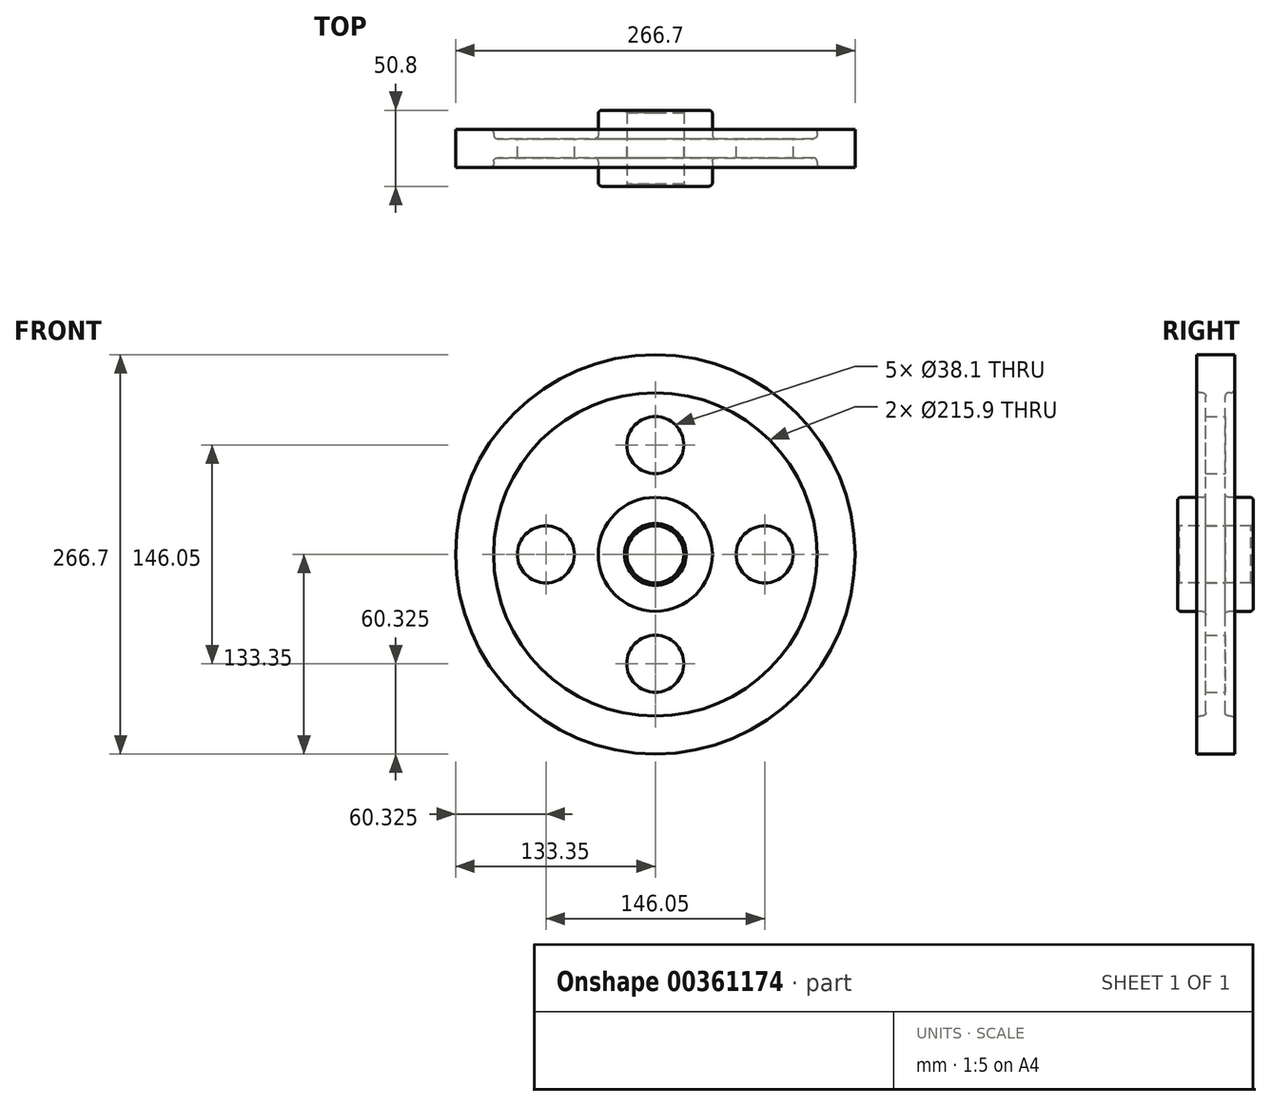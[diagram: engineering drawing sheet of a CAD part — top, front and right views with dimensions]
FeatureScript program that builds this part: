
annotation { "Feature Type Name" : "Feature", "Feature Type Description" : "" }
export const myFeature = defineFeature(function(context is Context, id is Id, definition is map)
    precondition{}
    {
        {
            var Q0;
            Q0=qCreatedBy(makeId("Right.planeOp"),FACE);
            var sketch = newSketch(context, id + "F0", { "sketchPlane" : qUnion([Q0])});
            skLineSegment(sketch, "E0", {"start": v(0, 0) * mm, "end": v(0, 28.58) * mm});
            skLineSegment(sketch, "E1", {"start": v(0, 28.58) * mm, "end": v(0, 73.03) * mm});
            skLineSegment(sketch, "E2", {"start": v(0, 73.03) * mm, "end": v(0, 120.65) * mm});
            skLineSegment(sketch, "E3", {"start": v(0, 0) * mm, "end": v(32.61, 0) * mm});
            skLineSegment(sketch, "E4.bottom", {"start": v(25.4, 19.05) * mm, "end": v(-25.4, 19.05) * mm});
            skLineSegment(sketch, "E4.top", {"start": v(25.4, 38.1) * mm, "end": v(6.35, 38.1) * mm});
            skLineSegment(sketch, "E4.left", {"start": v(25.4, 19.05) * mm, "end": v(25.4, 38.1) * mm});
            skLineSegment(sketch, "E4.right", {"start": v(-25.4, 19.05) * mm, "end": v(-25.4, 38.1) * mm});
            skPoint(sketch, "E4.middle", {"position": v(0, 28.58) * mm});
            skLineSegment(sketch, "E5.bottom", {"start": v(12.7, 107.95) * mm, "end": v(6.35, 107.95) * mm});
            skLineSegment(sketch, "E5.top", {"start": v(12.7, 133.35) * mm, "end": v(-12.7, 133.35) * mm});
            skLineSegment(sketch, "E5.left", {"start": v(12.7, 107.95) * mm, "end": v(12.7, 133.35) * mm});
            skLineSegment(sketch, "E5.right", {"start": v(-12.7, 107.95) * mm, "end": v(-12.7, 133.35) * mm});
            skPoint(sketch, "E5.middle", {"position": v(0, 120.65) * mm});
            skLineSegment(sketch, "E6.left", {"start": v(6.35, 35.07) * mm, "end": v(6.35, 110.98) * mm});
            skLineSegment(sketch, "E6.right", {"start": v(-6.35, 35.07) * mm, "end": v(-6.35, 110.98) * mm});
            skPoint(sketch, "E6.middle", {"position": v(0, 73.03) * mm});
            skLineSegment(sketch, "E7.trimOffspring", {"start": v(-6.35, 107.95) * mm, "end": v(-12.7, 107.95) * mm});
            skLineSegment(sketch, "E8.trimOffspring", {"start": v(-6.35, 38.1) * mm, "end": v(-25.4, 38.1) * mm});
            skSolve(sketch);
        }
        {
            var Q0;
            {var subQ4=sQuery(id+"F0.wireOp",EDGE,"E4.top");Q0=makeQuery(id+"F0.imprint","IMPRINT",FACE,{"disambiguationData":[TD([[makeQuery(id+"F0.imprint","IMPRINT",EDGE,{"derivedFrom":subQ4}),1.0]])]});}
            var Q1;
            Q1=sQuery(id+"F0.wireOp",EDGE,"E3");
            revolve(context, id + "F1", {"entities" : qUnion([Q0]), "axis" : qUnion([Q1]), "revolveType" : RevolveType.FULL});
        }
        {
            var Q0;
            Q0=makeQuery(id+"F1.opRevolve","SWEPT_FACE",FACE,{"disambiguationData":[OSD([sQuery(id+"F0.wireOp",EDGE,"E6.left")])]});
            var sketch = newSketch(context, id + "F2", { "sketchPlane" : qUnion([Q0])});
            skLineSegment(sketch, "E9", {"start": v(0, 0) * mm, "end": v(0, 73.03) * mm});
            skCircle(sketch, "E10", {"center": v(0, 73.03) * mm, "radius": 19.05 * mm});
            skCircle(sketch, "E11.1.0", {"center": v(-73.03, 0) * mm, "radius": 19.05 * mm});
            skCircle(sketch, "E11.2.0", {"center": v(0, -73.03) * mm, "radius": 19.05 * mm});
            skCircle(sketch, "E11.3.0", {"center": v(73.03, 0) * mm, "radius": 19.05 * mm});
            skPoint(sketch, "E11.center", {"position": v(0, 0) * mm});
            skSolve(sketch);
        }
        {
            var Q0;
            Q0=makeQuery(id+"F2.imprint","IMPRINT",FACE,{"disambiguationData":[TD([[makeQuery(id+"F2.imprint","IMPRINT",EDGE,{"derivedFrom":sQuery(id+"F2.wireOp",EDGE,"E10")}),1.0]])]});
            var Q1;
            Q1=makeQuery(id+"F2.imprint","IMPRINT",FACE,{"disambiguationData":[TD([[makeQuery(id+"F2.imprint","IMPRINT",EDGE,{"derivedFrom":sQuery(id+"F2.wireOp",EDGE,"E11.3.0")}),1.0]])]});
            var Q2;
            Q2=makeQuery(id+"F2.imprint","IMPRINT",FACE,{"disambiguationData":[TD([[makeQuery(id+"F2.imprint","IMPRINT",EDGE,{"derivedFrom":sQuery(id+"F2.wireOp",EDGE,"E11.2.0")}),1.0]])]});
            var Q3;
            Q3=makeQuery(id+"F2.imprint","IMPRINT",FACE,{"disambiguationData":[TD([[makeQuery(id+"F2.imprint","IMPRINT",EDGE,{"derivedFrom":sQuery(id+"F2.wireOp",EDGE,"E11.1.0")}),1.0]])]});
            extrude(context, id + "F3", {"entities" : qUnion([Q0, Q1, Q2, Q3]), "operationType" : NewBodyOperationType.REMOVE, "oppositeDirection" : true, "depth" : 25.4 * mm});
        }
        {
            var Q0;
            Q0=makeQuery(id+"F1.opRevolve","SWEPT_EDGE",EDGE,{"disambiguationData":[OSD([sQuery(id+"F0.wireOp",EDGE,"E6.right"),sQuery(id+"F0.wireOp",EDGE,"E7.trimOffspring")])]});
            var Q1;
            Q1=makeQuery(id+"F1.opRevolve","SWEPT_EDGE",EDGE,{"disambiguationData":[OSD([sQuery(id+"F0.wireOp",EDGE,"E5.right"),sQuery(id+"F0.wireOp",EDGE,"E7.trimOffspring")])]});
            var Q2;
            Q2=makeQuery(id+"F1.opRevolve","SWEPT_EDGE",EDGE,{"disambiguationData":[OSD([sQuery(id+"F0.wireOp",EDGE,"E4.right"),sQuery(id+"F0.wireOp",EDGE,"E8.trimOffspring")])]});
            var Q3;
            Q3=makeQuery(id+"F1.opRevolve","SWEPT_EDGE",EDGE,{"disambiguationData":[OSD([sQuery(id+"F0.wireOp",EDGE,"E6.right"),sQuery(id+"F0.wireOp",EDGE,"E8.trimOffspring")])]});
            var Q4;
            Q4=makeQuery(id+"F1.opRevolve","SWEPT_EDGE",EDGE,{"disambiguationData":[OSD([sQuery(id+"F0.wireOp",EDGE,"E4.top"),sQuery(id+"F0.wireOp",EDGE,"E4.left")])]});
            var Q5;
            Q5=makeQuery(id+"F1.opRevolve","SWEPT_EDGE",EDGE,{"disambiguationData":[OSD([sQuery(id+"F0.wireOp",EDGE,"E4.top"),sQuery(id+"F0.wireOp",EDGE,"E6.left")])]});
            var Q6;
            Q6=makeQuery(id+"F1.opRevolve","SWEPT_EDGE",EDGE,{"disambiguationData":[OSD([sQuery(id+"F0.wireOp",EDGE,"E5.bottom"),sQuery(id+"F0.wireOp",EDGE,"E5.left")])]});
            var Q7;
            Q7=makeQuery(id+"F1.opRevolve","SWEPT_EDGE",EDGE,{"disambiguationData":[OSD([sQuery(id+"F0.wireOp",EDGE,"E5.bottom"),sQuery(id+"F0.wireOp",EDGE,"E6.left")])]});
            fillet(context, id + "F4", {"entities" : qUnion([Q0, Q1, Q2, Q3, Q4, Q5, Q6, Q7]), "radius" : 2.54 * mm, "tangentPropagation" : true, "allowEdgeOverflow" : false});
        }
        {
            var Q0;
            Q0=makeQuery(id+"F1.opRevolve","SWEPT_EDGE",EDGE,{"disambiguationData":[OSD([sQuery(id+"F0.wireOp",EDGE,"E4.bottom"),sQuery(id+"F0.wireOp",EDGE,"E4.right")])]});
            var Q1;
            Q1=makeQuery(id+"F1.opRevolve","SWEPT_EDGE",EDGE,{"disambiguationData":[OSD([sQuery(id+"F0.wireOp",EDGE,"E4.bottom"),sQuery(id+"F0.wireOp",EDGE,"E4.left")])]});
            chamfer(context, id + "F5", {"entities" : qUnion([Q0, Q1]), "width" : 1.59 * mm, "tangentPropagation" : true});
        }
    });
